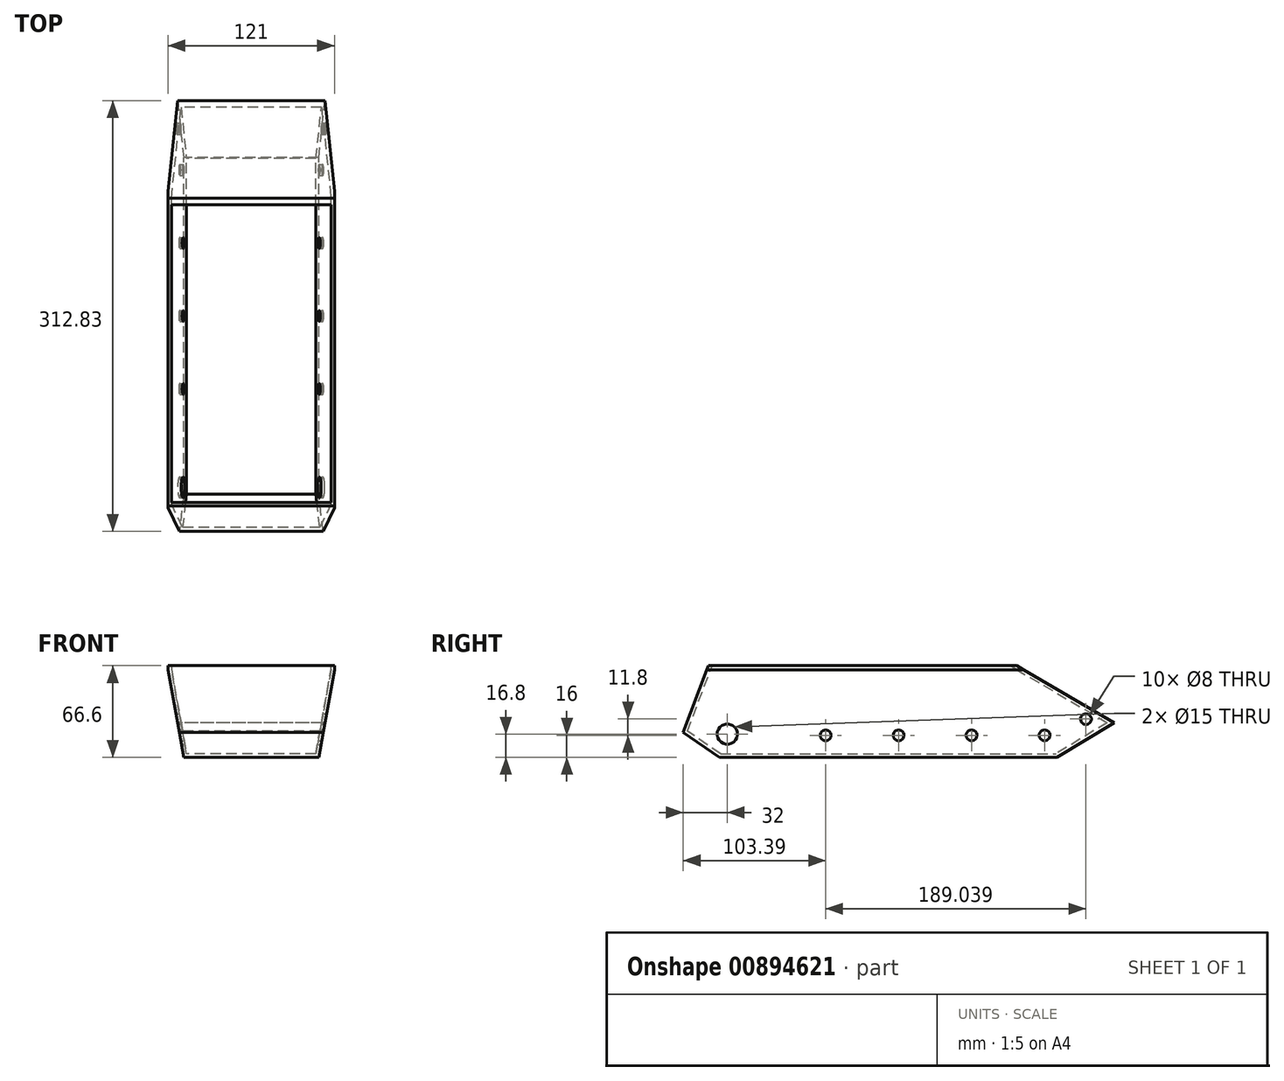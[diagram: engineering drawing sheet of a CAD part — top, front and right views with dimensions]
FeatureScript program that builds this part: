
annotation { "Feature Type Name" : "Feature", "Feature Type Description" : "" }
export const myFeature = defineFeature(function(context is Context, id is Id, definition is map)
    precondition{}
    {
        {
            var Q0;
            Q0=qCreatedBy(makeId("Front.planeOp"),FACE);
            var sketch = newSketch(context, id + "F0", { "sketchPlane" : qUnion([Q0])});
            skLineSegment(sketch, "E0", {"start": v(-49, -31.8) * mm, "end": v(49, -31.8) * mm});
            skLineSegment(sketch, "E1", {"start": v(49, -31.8) * mm, "end": v(60.5, 31.8) * mm});
            skLineSegment(sketch, "E2", {"start": v(-60.5, 31.8) * mm, "end": v(-49, -31.8) * mm});
            skLineSegment(sketch, "E3", {"start": v(60.5, 31.8) * mm, "end": v(60.5, 34.8) * mm});
            skLineSegment(sketch, "E4", {"start": v(60.5, 34.8) * mm, "end": v(-60.5, 34.8) * mm});
            skLineSegment(sketch, "E5", {"start": v(-60.5, 34.8) * mm, "end": v(-60.5, 31.8) * mm});
            skSolve(sketch);
        }
        {
            var Q0;
            Q0 = qSketchRegion(id + "F0", true);
            extrude(context, id + "F1", {"entities" : qUnion([Q0]), "endBound" : BoundingType.SYMMETRIC, "depth" : 600 * mm, "offsetDistance" : 25 * mm});
        }
        {
            var Q0;
            Q0=qCreatedBy(makeId("Right.planeOp"),FACE);
            var sketch = newSketch(context, id + "F2", { "sketchPlane" : qUnion([Q0])});
            skLineSegment(sketch, "E6", {"start": v(129.5, 34.8) * mm, "end": v(-94.24, 34.8) * mm});
            skLineSegment(sketch, "E7", {"start": v(-94.24, 34.8) * mm, "end": v(-112.55, -13.7) * mm});
            skLineSegment(sketch, "E8", {"start": v(-112.55, -13.7) * mm, "end": v(-86.16, -31.8) * mm});
            skLineSegment(sketch, "E9", {"start": v(-86.16, -31.8) * mm, "end": v(158.84, -31.8) * mm});
            skLineSegment(sketch, "E10", {"start": v(158.84, -31.8) * mm, "end": v(200.28, -6.6) * mm});
            skLineSegment(sketch, "E11", {"start": v(200.28, -6.6) * mm, "end": v(129.5, 34.8) * mm});
            skLineSegment(sketch, "E12.0", {"start": v(134.63, 31.8) * mm, "end": v(-95.37, 31.8) * mm});
            skSolve(sketch);
        }
        {
            var Q0;
            Q0 = qSketchRegion(id + "F2", true);
            extrude(context, id + "F3", {"entities" : qUnion([Q0]), "operationType" : NewBodyOperationType.INTERSECT, "endBound" : BoundingType.SYMMETRIC, "depth" : 150 * mm, "offsetDistance" : 25 * mm});
        }
        {
            var Q0;
            Q0=makeQuery(id+"F3.boolean.opBoolean","COPY",FACE,{"derivedFrom":makeQuery(id+"F3.boolean.toolComplement.opBoolean","COPY",FACE,{"derivedFrom":makeQuery(id+"F3.opExtrude","SWEPT_FACE",FACE,{"disambiguationData":[OSD([sQuery(id+"F2.wireOp",EDGE,"E11")])]})})});
            var Q1;
            Q1=makeQuery(id+"F1.opExtrude","SWEPT_FACE",FACE,{"disambiguationData":[OSD([sQuery(id+"F0.wireOp",EDGE,"E4")])]});
            var Q2;
            Q2=makeQuery(id+"F3.boolean.opBoolean","COPY",FACE,{"derivedFrom":makeQuery(id+"F3.boolean.toolComplement.opBoolean","COPY",FACE,{"derivedFrom":makeQuery(id+"F3.opExtrude","SWEPT_FACE",FACE,{"disambiguationData":[OSD([sQuery(id+"F2.wireOp",EDGE,"E7")])]})})});
            shell(context, id + "F4", {"entities" : qUnion([Q0, Q1, Q2]), "thickness" : 2.5 * mm});
        }
        {
            var Q0;
            Q0=qCreatedBy(makeId("Right.planeOp"),FACE);
            var sketch = newSketch(context, id + "F5", { "sketchPlane" : qUnion([Q0])});
            skCircle(sketch, "E13", {"center": v(179.88, -4) * mm, "radius": 4 * mm});
            skCircle(sketch, "E14", {"center": v(149.84, -15.8) * mm, "radius": 4 * mm});
            skCircle(sketch, "E15", {"center": v(96.84, -15.8) * mm, "radius": 4 * mm});
            skCircle(sketch, "E16", {"center": v(43.84, -15.8) * mm, "radius": 4 * mm});
            skCircle(sketch, "E17", {"center": v(-9.16, -15.8) * mm, "radius": 4 * mm});
            skCircle(sketch, "E18", {"center": v(-80.55, -15) * mm, "radius": 7.5 * mm});
            skSolve(sketch);
        }
        {
            var Q0;
            Q0 = qSketchRegion(id + "F5", true);
            extrude(context, id + "F6", {"entities" : qUnion([Q0]), "operationType" : NewBodyOperationType.REMOVE, "endBound" : BoundingType.SYMMETRIC, "oppositeDirection" : true, "depth" : 150 * mm, "offsetDistance" : 25 * mm});
        }
    });
